# Revit family: TCF23400AAA_TAC
name_source: partatom
category: Plumbing Fixtures
revit_build: Autodesk Revit 2018 (Build: 20170223_1515(x64)
units: mm (PartAtom-declared; Revit-internal decimal feet)

## family parameters
Always vertical = Yes
Cut with Voids When Loaded = No
OmniClass Number = 23.45.00.00
OmniClass Title = Sanitary, Laundry, and Cleaning Equipment
Part Type = Normal
Room Calculation Point = No
Round Connector Dimension = Use Diameter
Shared = No
Work Plane-Based = No

## types (1)
- TCF23400AAA_TAC
    CW Connection = Yes
    Description = Spray Seat WASHLET C2
    Finish = White
    HW Connection = No
    Height = 147 mm  [stored 0.482283 ft]
    Length = 483 mm  [stored 1.58465 ft]
    Manufacturer = TOTO LTD.
    Material = Plastic
    Model = TCF23400AAA
    URL = https://asia.toto.com
    Vent Connection = No
    Voltage = 220-240V
    Waste Connection = Yes
    Width = 472 mm

note: [stored X ft] marks values corroborated as IEEE doubles in the binary element streams (Revit-internal decimal feet)

## geometry (parser evidence)
native form markers: Sweep x2
no freeform markers — native parametric forms only
